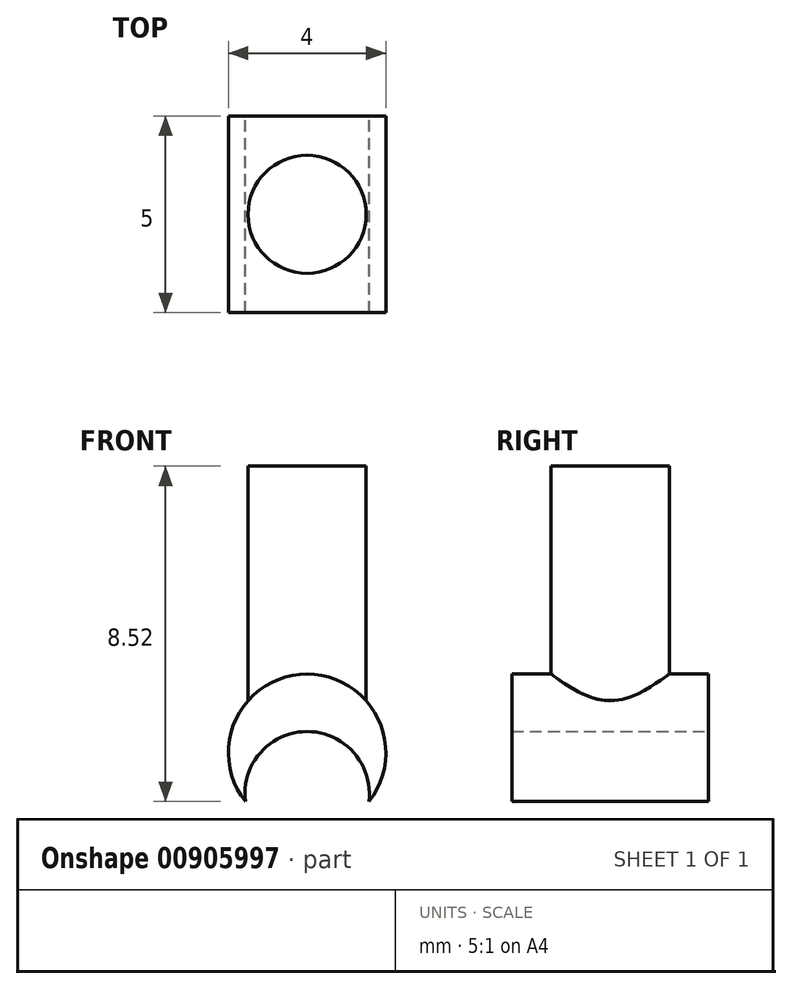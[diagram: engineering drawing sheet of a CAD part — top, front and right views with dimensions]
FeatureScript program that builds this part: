
annotation { "Feature Type Name" : "Feature", "Feature Type Description" : "" }
export const myFeature = defineFeature(function(context is Context, id is Id, definition is map)
    precondition{}
    {
        {
            var Q0;
            Q0=qCreatedBy(makeId("Front.planeOp"),FACE);
            var sketch = newSketch(context, id + "F0", { "sketchPlane" : qUnion([Q0])});
            skArc(sketch, "E0", {"start": v(1.57, -2.52) * mm, "mid": v(0, 0.72) * mm, "end": v(-1.57, -2.52) * mm});
            skArc(sketch, "E1", {"start": v(1.57, -2.52) * mm, "mid": v(0, -0.74) * mm, "end": v(-1.57, -2.52) * mm});
            skSolve(sketch);
        }
        {
            var Q0;
            Q0=makeQuery(id+"F0.imprint","IMPRINT",FACE,{"disambiguationData":[TD([[makeQuery(id+"F0.imprint","IMPRINT",EDGE,{"derivedFrom":sQuery(id+"F0.wireOp",EDGE,"E0")}),1.0]])]});
            extrude(context, id + "F1", {"entities" : qUnion([Q0]), "depth" : 5 * mm, "offsetDistance" : 25.4 * mm});
        }
        {
            var Q0;
            Q0=qCreatedBy(makeId("Top.planeOp"),FACE);
            var sketch = newSketch(context, id + "F2", { "sketchPlane" : qUnion([Q0])});
            skCircle(sketch, "E2", {"center": v(0, -2.5) * mm, "radius": 1.5 * mm});
            skSolve(sketch);
        }
        {
            var Q0;
            Q0 = qSketchRegion(id + "F2", true);
            extrude(context, id + "F3", {"entities" : qUnion([Q0]), "operationType" : NewBodyOperationType.ADD, "depth" : 6 * mm, "offsetDistance" : 25.4 * mm});
        }
    });
